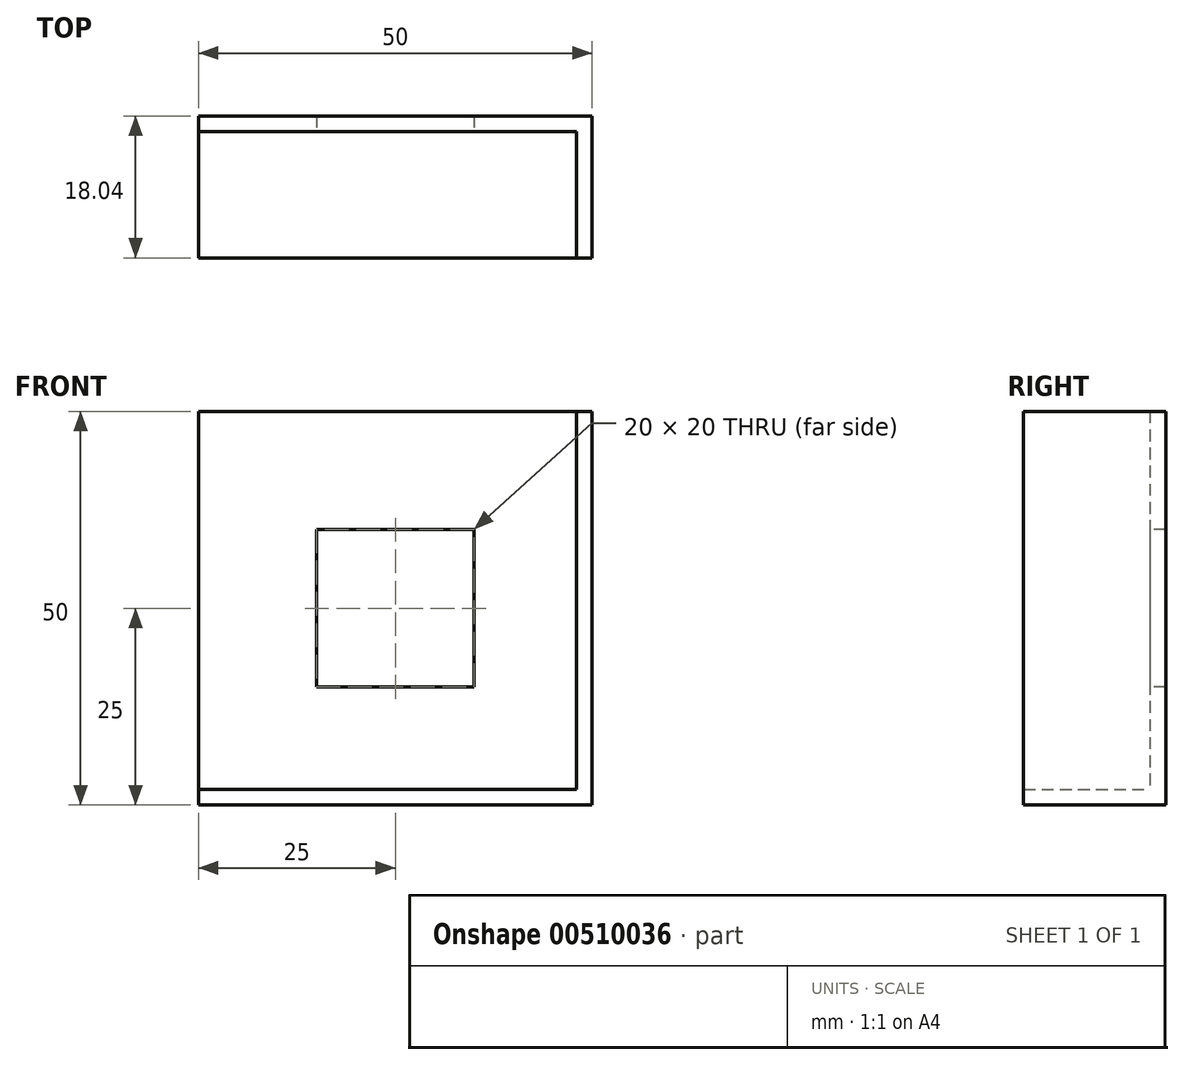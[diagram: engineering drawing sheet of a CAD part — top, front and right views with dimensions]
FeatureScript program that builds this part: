
annotation { "Feature Type Name" : "Feature", "Feature Type Description" : "" }
export const myFeature = defineFeature(function(context is Context, id is Id, definition is map)
    precondition{}
    {
        {
            var Q0;
            Q0=qCreatedBy(makeId("Front.planeOp"),FACE);
            var sketch = newSketch(context, id + "F0", { "sketchPlane" : qUnion([Q0])});
            skLineSegment(sketch, "E0.bottom", {"start": v(0, 0) * mm, "end": v(50, 0) * mm});
            skLineSegment(sketch, "E0.top", {"start": v(0, 50) * mm, "end": v(50, 50) * mm});
            skLineSegment(sketch, "E0.left", {"start": v(0, 0) * mm, "end": v(0, 50) * mm});
            skLineSegment(sketch, "E0.right", {"start": v(50, 0) * mm, "end": v(50, 50) * mm});
            skSolve(sketch);
        }
        {
            var Q0;
            Q0=makeQuery(id+"F0.imprint","IMPRINT",FACE,{"disambiguationData":[TD([[makeQuery(id+"F0.imprint","IMPRINT",EDGE,{"derivedFrom":sQuery(id+"F0.wireOp",EDGE,"E0.bottom")}),1.0]])]});
            var sketch = newSketch(context, id + "F1", { "sketchPlane" : qUnion([Q0])});
            skSolve(sketch);
        }
        {
            var Q0;
            Q0 = qSketchRegion(id + "F1", true);
            var Q1;
            Q1=makeQuery(id+"F0.imprint","IMPRINT",FACE,{"disambiguationData":[TD([[makeQuery(id+"F0.imprint","IMPRINT",EDGE,{"derivedFrom":sQuery(id+"F0.wireOp",EDGE,"E0.bottom")}),1.0]])]});
            extrude(context, id + "F2", {"entities" : qUnion([Q0, Q1]), "depth" : 2 * mm});
        }
        {
            var Q0;
            Q0=makeQuery(id+"F2.opExtrude","CAP_FACE",FACE,{"disambiguationData":[OSD([sQuery(id+"F0.wireOp",EDGE,"E0.bottom"),sQuery(id+"F0.wireOp",EDGE,"E0.top"),sQuery(id+"F0.wireOp",EDGE,"E0.left"),sQuery(id+"F0.wireOp",EDGE,"E0.right")])],"isStart":false});
            var sketch = newSketch(context, id + "F3", { "sketchPlane" : qUnion([Q0])});
            skLineSegment(sketch, "E1.bottom", {"start": v(15, 35) * mm, "end": v(35, 35) * mm});
            skLineSegment(sketch, "E1.top", {"start": v(15, 15) * mm, "end": v(35, 15) * mm});
            skLineSegment(sketch, "E1.left", {"start": v(15, 35) * mm, "end": v(15, 15) * mm});
            skLineSegment(sketch, "E1.right", {"start": v(35, 35) * mm, "end": v(35, 15) * mm});
            skSolve(sketch);
        }
        {
            var Q0;
            Q0=makeQuery(id+"F3.imprint","IMPRINT",FACE,{"disambiguationData":[TD([[makeQuery(id+"F3.imprint","IMPRINT",EDGE,{"derivedFrom":sQuery(id+"F3.wireOp",EDGE,"E1.bottom")}),-1.0]])]});
            extrude(context, id + "F4", {"entities" : qUnion([Q0]), "operationType" : NewBodyOperationType.REMOVE, "oppositeDirection" : true, "depth" : 25 * mm});
        }
        {
            var Q0;
            Q0=makeQuery(id+"F2.opExtrude","SWEPT_FACE",FACE,{"disambiguationData":[OSD([sQuery(id+"F0.wireOp",EDGE,"E0.bottom")])]});
            var sketch = newSketch(context, id + "F5", { "sketchPlane" : qUnion([Q0])});
            skLineSegment(sketch, "E2.bottom", {"start": v(50, 2) * mm, "end": v(47.71, 2) * mm});
            skLineSegment(sketch, "E2.top", {"start": v(50, 2) * mm, "end": v(47.71, 2) * mm});
            skLineSegment(sketch, "E2.left", {"start": v(50, 2) * mm, "end": v(50, 2) * mm});
            skLineSegment(sketch, "E2.right", {"start": v(47.71, 2) * mm, "end": v(47.71, 2) * mm});
            skLineSegment(sketch, "E3.bottom", {"start": v(50, 18.04) * mm, "end": v(48, 18.04) * mm});
            skLineSegment(sketch, "E3.top", {"start": v(50, 2) * mm, "end": v(48, 2) * mm});
            skLineSegment(sketch, "E3.left", {"start": v(50, 18.04) * mm, "end": v(50, 2) * mm});
            skLineSegment(sketch, "E3.right", {"start": v(48, 18.04) * mm, "end": v(48, 2) * mm});
            skSolve(sketch);
        }
        {
            var Q0;
            Q0=makeQuery(id+"F5.imprint","IMPRINT",FACE,{"disambiguationData":[TD([[makeQuery(id+"F5.imprint","IMPRINT",EDGE,{"derivedFrom":sQuery(id+"F5.wireOp",EDGE,"E3.bottom")}),1.0]])]});
            var Q1;
            Q1=makeQuery(id+"F2.opExtrude","SWEPT_FACE",FACE,{"disambiguationData":[OSD([sQuery(id+"F0.wireOp",EDGE,"E0.top")])]});
            extrude(context, id + "F6", {"entities" : qUnion([Q0]), "operationType" : NewBodyOperationType.ADD, "endBound" : BoundingType.UP_TO_SURFACE, "oppositeDirection" : true, "endBoundEntityFace" : qUnion([Q1]), "depth" : 25 * mm});
        }
        {
            var Q0;
            Q0=makeQuery(id+"F2.opExtrude","SWEPT_FACE",FACE,{"disambiguationData":[OSD([sQuery(id+"F0.wireOp",EDGE,"E0.left")])]});
            var sketch = newSketch(context, id + "F7", { "sketchPlane" : qUnion([Q0])});
            skLineSegment(sketch, "E4.bottom", {"start": v(0, 0) * mm, "end": v(10.73, 0) * mm});
            skLineSegment(sketch, "E4.top", {"start": v(0, 2) * mm, "end": v(10.73, 2) * mm});
            skLineSegment(sketch, "E4.left", {"start": v(0, 0) * mm, "end": v(0, 2) * mm});
            skLineSegment(sketch, "E4.right", {"start": v(10.73, 0) * mm, "end": v(10.73, 2) * mm});
            skSolve(sketch);
        }
        {
            var Q0;
            {var subQ3=sQuery(id+"F7.wireOp",EDGE,"E4.right");Q0=makeQuery(id+"F7.imprint","IMPRINT",FACE,{"disambiguationData":[TD([[makeQuery(id+"F7.imprint","IMPRINT",EDGE,{"derivedFrom":subQ3}),1.0]])]});}
            extrude(context, id + "F8", {"entities" : qUnion([Q0]), "operationType" : NewBodyOperationType.ADD, "endBound" : BoundingType.UP_TO_NEXT, "oppositeDirection" : true, "depth" : 25 * mm});
        }
        {
            var Q0;
            Q0=makeQuery(id+"F8.opExtrude","SWEPT_FACE",FACE,{"disambiguationData":[OSD([sQuery(id+"F7.wireOp",EDGE,"E4.right")])]});
            var Q1;
            Q1=makeQuery(id+"F6.opExtrude","SWEPT_FACE",FACE,{"disambiguationData":[OSD([sQuery(id+"F5.wireOp",EDGE,"E3.bottom")])]});
            extrude(context, id + "F9", {"entities" : qUnion([Q0]), "operationType" : NewBodyOperationType.ADD, "endBound" : BoundingType.UP_TO_SURFACE, "endBoundEntityFace" : qUnion([Q1]), "depth" : 25 * mm});
        }
    });
